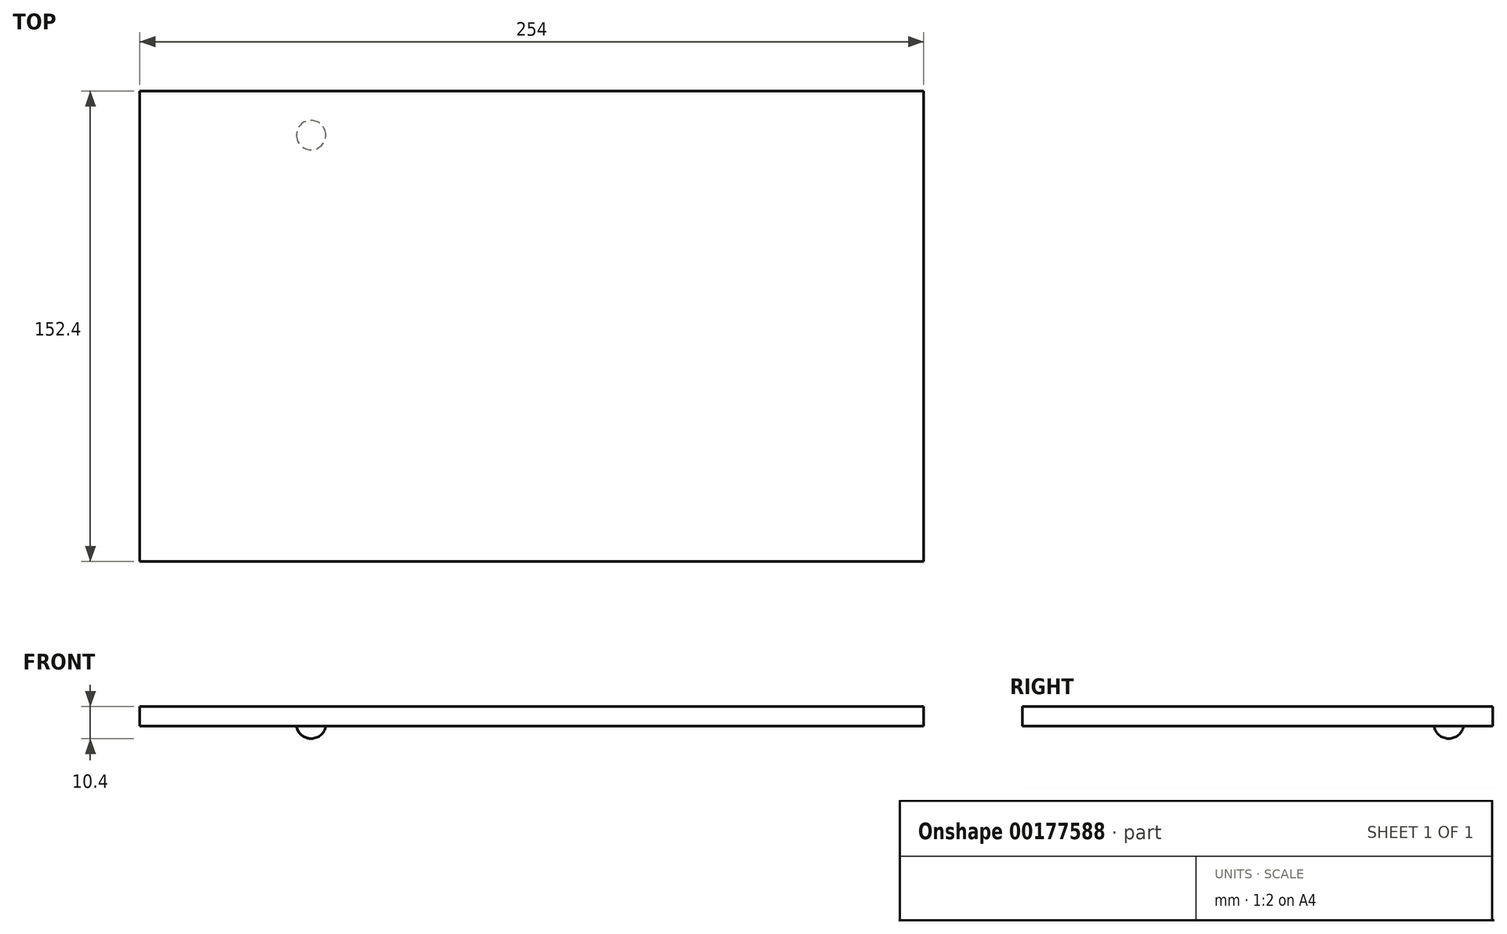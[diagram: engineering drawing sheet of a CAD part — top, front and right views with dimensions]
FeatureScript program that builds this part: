
annotation { "Feature Type Name" : "Feature", "Feature Type Description" : "" }
export const myFeature = defineFeature(function(context is Context, id is Id, definition is map)
    precondition{}
    {
        {
            var Q0;
            Q0=qCreatedBy(makeId("Top.planeOp"),FACE);
            var sketch = newSketch(context, id + "F0", { "sketchPlane" : qUnion([Q0])});
            skLineSegment(sketch, "E0.bottom", {"start": v(-127, 76.2) * mm, "end": v(127, 76.2) * mm});
            skLineSegment(sketch, "E0.top", {"start": v(-127, -76.2) * mm, "end": v(127, -76.2) * mm});
            skLineSegment(sketch, "E0.left", {"start": v(-127, 76.2) * mm, "end": v(-127, -76.2) * mm});
            skLineSegment(sketch, "E0.right", {"start": v(127, 76.2) * mm, "end": v(127, -76.2) * mm});
            skPoint(sketch, "E0.middle", {"position": v(0, 0) * mm});
            skSolve(sketch);
        }
        {
            var Q0;
            Q0 = qSketchRegion(id + "F0", true);
            extrude(context, id + "F1", {"entities" : qUnion([Q0]), "depth" : 6.35 * mm});
        }
        {
            var Q0;
            Q0=makeQuery(id+"F1.opExtrude","CAP_FACE",FACE,{"disambiguationData":[OSD([sQuery(id+"F0.wireOp",EDGE,"E0.bottom"),sQuery(id+"F0.wireOp",EDGE,"E0.top"),sQuery(id+"F0.wireOp",EDGE,"E0.left"),sQuery(id+"F0.wireOp",EDGE,"E0.right")])],"isStart":true});
            var sketch = newSketch(context, id + "F2", { "sketchPlane" : qUnion([Q0])});
            skPoint(sketch, "E1.first.point", {"position": v(0, 61.91) * mm});
            skPoint(sketch, "E1.second.point", {"position": v(-71.5, -61.91) * mm});
            skPoint(sketch, "E1.third.point", {"position": v(71.5, -61.91) * mm});
            skLineSegment(sketch, "E2", {"start": v(-71.5, -61.91) * mm, "end": v(71.5, -61.91) * mm, "construction": true});
            skCircle(sketch, "E3", {"center": v(0, 61.91) * mm, "radius": 4.76 * mm});
            skCircle(sketch, "E4", {"center": v(-71.5, -61.91) * mm, "radius": 4.76 * mm});
            skCircle(sketch, "E5", {"center": v(71.5, -61.91) * mm, "radius": 4.76 * mm});
            skLineSegment(sketch, "E6", {"start": v(0, 61.91) * mm, "end": v(-71.5, -61.91) * mm, "construction": true});
            skLineSegment(sketch, "E7", {"start": v(0, 61.91) * mm, "end": v(71.5, -61.91) * mm, "construction": true});
            skCircle(sketch, "E8", {"center": v(0, -20.64) * mm, "radius": 82.55 * mm, "construction": true});
            skLineSegment(sketch, "E9", {"start": v(0, 61.91) * mm, "end": v(0, -61.91) * mm, "construction": true});
            skSolve(sketch);
        }
        {
            var Q0;
            Q0=sQuery(id+"F2.wireOp",EDGE,"E2");
            var Q1;
            Q1=makeQuery(id+"F2.imprint","IMPRINT",FACE,{"disambiguationData":[TD([[makeQuery(id+"F2.imprint","IMPRINT",EDGE,{"derivedFrom":sQuery(id+"F2.wireOp",EDGE,"E3")}),-1.0]])]});
            cPlane(context, id + "F3", {"entities" : qUnion([Q0, Q1]), "cplaneType" : CPlaneType.LINE_ANGLE, "offset" : 25.4 * mm, "angle" : 90 * degree, "width" : 152.4 * mm, "height" : 152.4 * mm});
        }
        {
            var Q0;
            Q0=qCreatedBy(id+"F3.planeOp",FACE);
            var sketch = newSketch(context, id + "F4", { "sketchPlane" : qUnion([Q0])});
            skArc(sketch, "E10", {"start": v(-71.5, -4.05) * mm, "mid": v(-68.08, -2.63) * mm, "end": v(-66.66, 0.78) * mm});
            skLineSegment(sketch, "E11", {"start": v(-71.5, -4.05) * mm, "end": v(-71.5, 0.78) * mm});
            skLineSegment(sketch, "E12", {"start": v(-71.5, 0.78) * mm, "end": v(-66.66, 0.78) * mm});
            skLineSegment(sketch, "E13.0", {"start": v(-66.73, 0) * mm, "end": v(-76.25, 0) * mm, "construction": true});
            skSolve(sketch);
        }
        {
            var Q0;
            Q0=makeQuery(id+"F4.imprint","IMPRINT",FACE,{"disambiguationData":[TD([[makeQuery(id+"F4.imprint","IMPRINT",EDGE,{"derivedFrom":sQuery(id+"F4.wireOp",EDGE,"E10")}),1.0]])]});
            var Q1;
            Q1=sQuery(id+"F4.wireOp",EDGE,"E11");
            revolve(context, id + "F5", {"operationType" : NewBodyOperationType.ADD, "entities" : qUnion([Q0]), "axis" : qUnion([Q1]), "revolveType" : RevolveType.FULL});
        }
        {
            var Q0;
            Q0=qCreatedBy(makeId("Right.planeOp"),FACE);
            var sketch = newSketch(context, id + "F6", { "sketchPlane" : qUnion([Q0])});
            skLineSegment(sketch, "E14", {"start": v(20.64, 0) * mm, "end": v(20.64, -39.13) * mm, "construction": true});
            skSolve(sketch);
        }
    });
